# Revit family: 511_2H_AWN-UT_stucco key
name_source: partatom
category: Windows
revit_build: Autodesk Revit 2016 (Build: 20150220_1215(x64)
units: mm (PartAtom-declared; Revit-internal decimal feet)

## family parameters
Always vertical = Yes
Cut with Voids When Loaded = No
Host = Wall
OmniClass Number = 23.30.20.00
OmniClass Title = Windows
Room Calculation Point = No
Shared = No

## types (96) — shared parameters
Default Sill Height = 31 1/2"
MLWC = 3 9/16"
MLWE = 3 1/4"
Wall Closure = By host

## per-type parameters (varying)
| type | HBS | Height | MLCL | MLCR | MLW | VBS | Width |
| 30x24Min | 12" | 24" | 7 1/2" | 7 1/2" | 1 7/8" | 15" | 30" |
| 72x72 | 30" | 72" | 18" | 18" | 4 1/2" | 36" | 72" |
| 96x96Max | 32" | 96" | 24" | 24" | 6" | 48" | 96" |
| 36x36 | 15" | 36" | 9" | 9" | 2 1/4" | 18" | 36" |
| 48x48 | 20" | 48" | 12" | 12" | 3" | 24" | 48" |
| 60x60 | 30" | 60" | 15" | 15" | 3 3/4" | 30" | 60" |
| 84x84 | 32" | 84" | 21" | 21" | 5 1/4" | 42" | 84" |
| 30x30 | 15" | 30" | 7 1/2" | 7 1/2" | 1 7/8" | 15" | 30" |
| 30x36 | 15" | 36" | 7 1/2" | 7 1/2" | 1 7/8" | 15" | 30" |
| 30x42 | 15" | 42" | 7 1/2" | 7 1/2" | 1 7/8" | 15" | 30" |
| 30x48 | 15" | 48" | 7 1/2" | 7 1/2" | 1 7/8" | 15" | 30" |
| 30x54 | 15" | 54" | 7 1/2" | 7 1/2" | 1 7/8" | 15" | 30" |
| 36x24 | 12" | 24" | 9" | 9" | 2 1/4" | 18" | 36" |
| 36x30 | 15" | 30" | 9" | 9" | 2 1/4" | 18" | 36" |
| 36x42 | 18" | 42" | 9" | 9" | 2 1/4" | 18" | 36" |
| 36x48 | 24" | 48" | 9" | 9" | 2 1/4" | 18" | 36" |
| 36x54 | 24" | 54" | 9" | 9" | 2 1/4" | 18" | 36" |
| 36x60 | 24" | 60" | 9" | 9" | 2 1/4" | 18" | 36" |
| 42x24 | 12" | 24" | 10 1/2" | 10 1/2" | 2 5/8" | 21" | 42" |
| 42x30 | 15" | 30" | 10 1/2" | 10 1/2" | 2 5/8" | 21" | 42" |
| 42x36 | 15" | 36" | 10 1/2" | 10 1/2" | 2 5/8" | 21" | 42" |
| 42x42 | 18" | 42" | 10 1/2" | 10 1/2" | 2 5/8" | 21" | 42" |
| 42x48 | 24" | 48" | 10 1/2" | 10 1/2" | 2 5/8" | 21" | 42" |
| 42x54 | 30" | 54" | 10 1/2" | 10 1/2" | 2 5/8" | 21" | 42" |
| 42x60 | 32" | 60" | 10 1/2" | 10 1/2" | 2 5/8" | 21" | 42" |
| 42x66 | 32" | 66" | 10 1/2" | 10 1/2" | 2 5/8" | 21" | 42" |
| 42x72 | 32" | 72" | 10 1/2" | 10 1/2" | 2 5/8" | 21" | 42" |
| 48x42 | 20" | 42" | 12" | 12" | 3" | 24" | 48" |
| 48x36 | 20" | 36" | 12" | 12" | 3" | 24" | 48" |
| 48x30 | 15" | 30" | 12" | 12" | 3" | 24" | 48" |
| 48x54 | 24" | 54" | 12" | 12" | 3" | 24" | 48" |
| 48x60 | 30" | 60" | 12" | 12" | 3" | 24" | 48" |
| 48x66 | 32" | 66" | 12" | 12" | 3" | 24" | 48" |
| 48x72 | 32" | 72" | 12" | 12" | 3" | 24" | 48" |
| 54x30 | 15" | 30" | 13 1/2" | 13 1/2" | 3 3/8" | 27" | 54" |
| 54x36 | 15" | 36" | 13 1/2" | 13 1/2" | 3 3/8" | 27" | 54" |
| 54x42 | 18" | 42" | 13 1/2" | 13 1/2" | 3 3/8" | 27" | 54" |
| 54x48 | 24" | 48" | 13 1/2" | 13 1/2" | 3 3/8" | 27" | 54" |
| 54x54 | 24" | 54" | 13 1/2" | 13 1/2" | 3 3/8" | 27" | 54" |
| 54x60 | 30" | 60" | 13 1/2" | 13 1/2" | 3 3/8" | 27" | 54" |
| 54x66 | 32" | 66" | 13 1/2" | 13 1/2" | 3 3/8" | 27" | 54" |
| 54x72 | 32" | 72" | 13 1/2" | 13 1/2" | 3 3/8" | 27" | 54" |
| 54x78 | 32" | 78" | 13 1/2" | 13 1/2" | 3 3/8" | 27" | 54" |
| 54x84 | 32" | 84" | 13 1/2" | 13 1/2" | 3 3/8" | 27" | 54" |
| 60x36 | 15" | 36" | 15" | 15" | 3 3/4" | 30" | 60" |
| 60x42 | 18" | 42" | 15" | 15" | 3 3/4" | 30" | 60" |
| 60x48 | 24" | 48" | 15" | 15" | 3 3/4" | 30" | 60" |
| 60x54 | 24" | 54" | 15" | 15" | 3 3/4" | 30" | 60" |
| 60x66 | 32" | 66" | 15" | 15" | 3 3/4" | 30" | 60" |
| 60x72 | 32" | 72" | 15" | 15" | 3 3/4" | 30" | 60" |
| 60x78 | 32" | 78" | 15" | 15" | 3 3/4" | 30" | 60" |
| 60x84 | 32" | 84" | 15" | 15" | 3 3/4" | 30" | 60" |
| 66x36 | 15" | 36" | 16 1/2" | 16 1/2" | 4 1/8" | 33" | 66" |
| 66x42 | 18" | 42" | 16 1/2" | 16 1/2" | 4 1/8" | 33" | 66" |
| 66x48 | 24" | 48" | 16 1/2" | 16 1/2" | 4 1/8" | 33" | 66" |
| 66x54 | 24" | 54" | 16 1/2" | 16 1/2" | 4 1/8" | 33" | 66" |
| 66x60 | 30" | 60" | 16 1/2" | 16 1/2" | 4 1/8" | 33" | 66" |
| 66x66 | 32" | 66" | 16 1/2" | 16 1/2" | 4 1/8" | 33" | 66" |
| 66x72 | 32" | 72" | 16 1/2" | 16 1/2" | 4 1/8" | 33" | 66" |
| 66x78 | 32" | 78" | 16 1/2" | 16 1/2" | 4 1/8" | 33" | 66" |
| 66x84 | 32" | 84" | 16 1/2" | 16 1/2" | 4 1/8" | 33" | 66" |
| 66x90 | 32" | 90" | 16 1/2" | 16 1/2" | 4 1/8" | 33" | 66" |
| 72x42 | 18" | 42" | 18" | 18" | 4 1/2" | 36" | 72" |
| 72x48 | 24" | 48" | 18" | 18" | 4 1/2" | 36" | 72" |
| 72x54 | 24" | 54" | 18" | 18" | 4 1/2" | 36" | 72" |
| 72x60 | 30" | 60" | 18" | 18" | 4 1/2" | 36" | 72" |
| 72x66 | 32" | 66" | 18" | 18" | 4 1/2" | 36" | 72" |
| 72x78 | 32" | 78" | 18" | 18" | 4 1/2" | 36" | 72" |
| 72x84 | 32" | 84" | 18" | 18" | 4 1/2" | 36" | 72" |
| 72x90 | 32" | 90" | 18" | 18" | 4 1/2" | 36" | 72" |
| 72x96 | 32" | 96" | 18" | 18" | 4 1/2" | 36" | 72" |
| 78x42 | 18" | 42" | 19 1/2" | 19 1/2" | 4 7/8" | 39" | 78" |
| 78x48 | 24" | 48" | 19 1/2" | 19 1/2" | 4 7/8" | 39" | 78" |
| 78x54 | 24" | 54" | 19 1/2" | 19 1/2" | 4 7/8" | 39" | 78" |
| 78x60 | 30" | 60" | 19 1/2" | 19 1/2" | 4 7/8" | 39" | 78" |
| 78x66 | 32" | 66" | 19 1/2" | 19 1/2" | 4 7/8" | 39" | 78" |
| 78x72 | 32" | 72" | 19 1/2" | 19 1/2" | 4 7/8" | 39" | 78" |
| 78x78 | 32" | 78" | 19 1/2" | 19 1/2" | 4 7/8" | 39" | 78" |
| 78x84 | 32" | 84" | 19 1/2" | 19 1/2" | 4 7/8" | 39" | 78" |
| 78x90 | 32" | 90" | 19 1/2" | 19 1/2" | 4 7/8" | 39" | 78" |
| 78x96 | 32" | 96" | 19 1/2" | 19 1/2" | 4 7/8" | 39" | 78" |
| 84x48 | 24" | 48" | 21" | 21" | 5 1/4" | 42" | 84" |
| 84x54 | 24" | 54" | 21" | 21" | 5 1/4" | 42" | 84" |
| 84x60 | 30" | 60" | 21" | 21" | 5 1/4" | 42" | 84" |
| 84x66 | 32" | 66" | 21" | 21" | 5 1/4" | 42" | 84" |
| 84x72 | 32" | 72" | 21" | 21" | 5 1/4" | 42" | 84" |
| 84x78 | 32" | 78" | 21" | 21" | 5 1/4" | 42" | 84" |
| 84x90 | 32" | 90" | 21" | 21" | 5 1/4" | 42" | 84" |
| 84x96 | 32" | 96" | 21" | 21" | 5 1/4" | 42" | 84" |
| 96x54 | 24" | 54" | 24" | 24" | 6" | 48" | 96" |
| 96x60 | 30" | 60" | 24" | 24" | 6" | 48" | 96" |
| 96x66 | 32" | 66" | 24" | 24" | 6" | 48" | 96" |
| 96x72 | 32" | 72" | 24" | 24" | 6" | 48" | 96" |
| 96x78 | 32" | 78" | 24" | 24" | 6" | 48" | 96" |
| 96x84 | 32" | 84" | 24" | 24" | 6" | 48" | 96" |
| 96x90 | 32" | 90" | 24" | 24" | 6" | 48" | 96" |

## geometry (parser evidence)
native form markers: Sweep x3
no freeform markers — native parametric forms only
